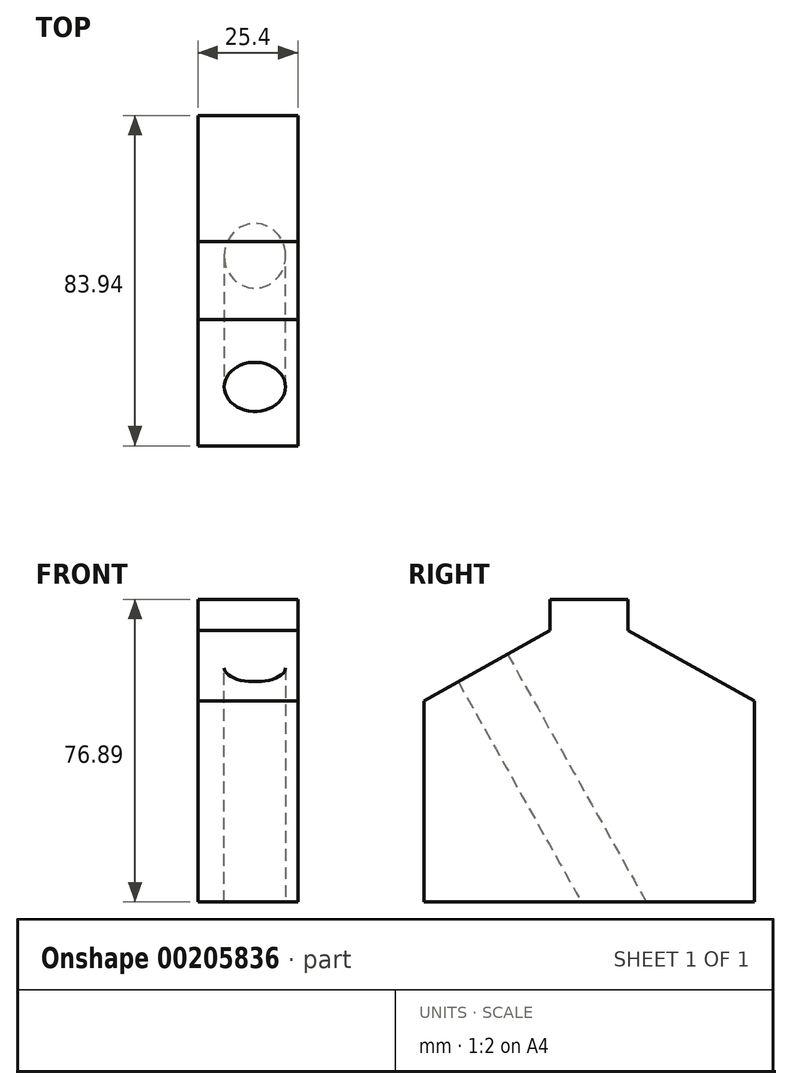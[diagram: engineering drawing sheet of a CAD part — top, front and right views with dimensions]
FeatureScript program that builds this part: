
annotation { "Feature Type Name" : "Feature", "Feature Type Description" : "" }
export const myFeature = defineFeature(function(context is Context, id is Id, definition is map)
    precondition{}
    {
        {
            var Q0;
            Q0=qCreatedBy(makeId("Right.planeOp"),FACE);
            var sketch = newSketch(context, id + "F0", { "sketchPlane" : qUnion([Q0])});
            skLineSegment(sketch, "E0", {"start": v(-9.89, 51.36) * mm, "end": v(-9.89, 43.49) * mm});
            skLineSegment(sketch, "E1", {"start": v(-9.89, 43.49) * mm, "end": v(-41.97, 25.53) * mm});
            skLineSegment(sketch, "E2", {"start": v(-41.97, 25.53) * mm, "end": v(-41.97, -25.53) * mm});
            skLineSegment(sketch, "E3", {"start": v(-41.97, -25.53) * mm, "end": v(0, -25.53) * mm});
            skLineSegment(sketch, "E4", {"start": v(-9.89, 51.36) * mm, "end": v(0, 51.36) * mm});
            skLineSegment(sketch, "E5.MirrorCS", {"start": v(9.89, 51.36) * mm, "end": v(0, 51.36) * mm});
            skLineSegment(sketch, "E6.MirrorCS", {"start": v(9.89, 51.36) * mm, "end": v(9.89, 43.49) * mm});
            skLineSegment(sketch, "E7.MirrorCS", {"start": v(9.89, 43.49) * mm, "end": v(41.97, 25.53) * mm});
            skLineSegment(sketch, "E8.MirrorCS", {"start": v(41.97, 25.53) * mm, "end": v(41.97, -25.53) * mm});
            skLineSegment(sketch, "E9.MirrorCS", {"start": v(41.97, -25.53) * mm, "end": v(0, -25.53) * mm});
            skSolve(sketch);
        }
        {
            var Q0;
            Q0=makeQuery(id+"F0.imprint","IMPRINT",FACE,{"disambiguationData":[TD([[makeQuery(id+"F0.imprint","IMPRINT",EDGE,{"derivedFrom":sQuery(id+"F0.wireOp",EDGE,"E0")}),1.0]])]});
            extrude(context, id + "F1", {"entities" : qUnion([Q0]), "depth" : 25.4 * mm});
        }
        {
            var Q0;
            Q0=makeQuery(id+"F1.opExtrude","SWEPT_FACE",FACE,{"disambiguationData":[OSD([sQuery(id+"F0.wireOp",EDGE,"E1")])]});
            var sketch = newSketch(context, id + "F2", { "sketchPlane" : qUnion([Q0])});
            skEllipse(sketch, "E10", {"center": v(14.48, -6.96) * mm, "majorRadius": 7.82 * mm, "minorRadius": 7.17 * mm, "majorAxis": v(-1, 0)});
            skSolve(sketch);
        }
        {
            var Q0;
            Q0=makeQuery(id+"F2.imprint","IMPRINT",FACE,{"disambiguationData":[TD([[makeQuery(id+"F2.imprint","IMPRINT",EDGE,{"derivedFrom":sQuery(id+"F2.wireOp",EDGE,"E10")}),1.0]])]});
            extrude(context, id + "F3", {"entities" : qUnion([Q0]), "operationType" : NewBodyOperationType.REMOVE, "oppositeDirection" : true, "depth" : 99.31 * mm});
        }
    });
